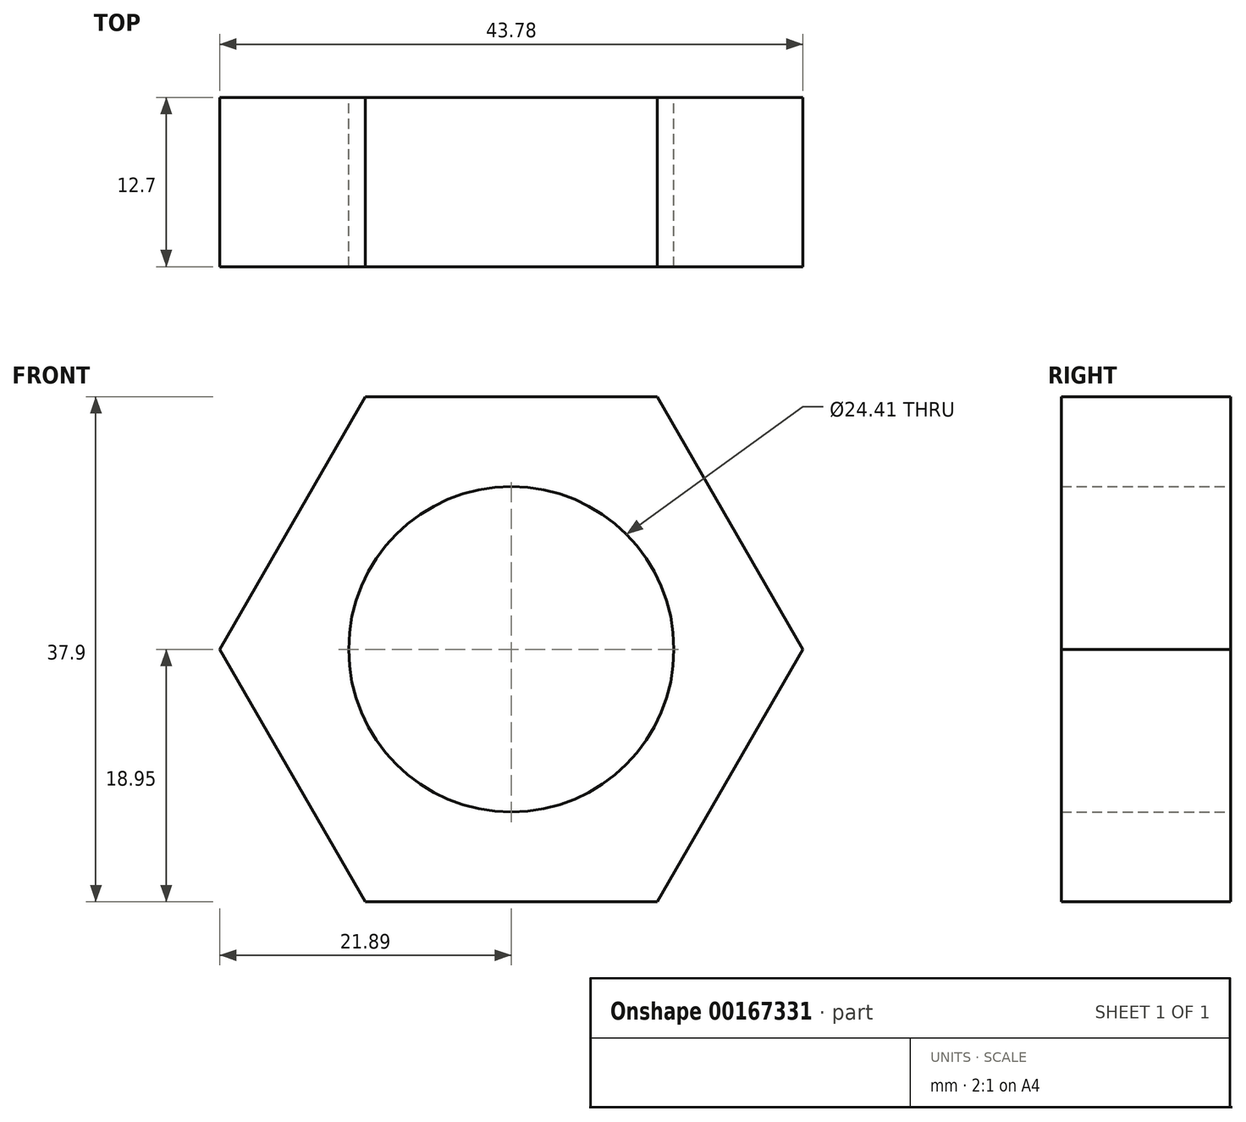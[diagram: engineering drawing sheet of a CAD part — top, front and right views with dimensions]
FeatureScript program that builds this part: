
annotation { "Feature Type Name" : "Feature", "Feature Type Description" : "" }
export const myFeature = defineFeature(function(context is Context, id is Id, definition is map)
    precondition{}
    {
        {
            var Q0;
            Q0=qCreatedBy(makeId("Front.planeOp"),FACE);
            var sketch = newSketch(context, id + "F0", { "sketchPlane" : qUnion([Q0])});
            skCircle(sketch, "E0.cCircle", {"center": v(0, 0) * mm, "radius": 18.95 * mm, "construction": true});
            skLineSegment(sketch, "E0.0", {"start": v(-10.94, 18.95) * mm, "end": v(10.94, 18.95) * mm});
            skLineSegment(sketch, "E0.1", {"start": v(10.94, 18.95) * mm, "end": v(21.89, 0) * mm});
            skLineSegment(sketch, "E0.2", {"start": v(21.89, 0) * mm, "end": v(10.94, -18.95) * mm});
            skLineSegment(sketch, "E0.3", {"start": v(10.94, -18.95) * mm, "end": v(-10.94, -18.95) * mm});
            skLineSegment(sketch, "E0.4", {"start": v(-10.94, -18.95) * mm, "end": v(-21.89, 0) * mm});
            skLineSegment(sketch, "E0.5", {"start": v(-21.89, 0) * mm, "end": v(-10.94, 18.95) * mm});
            skPoint(sketch, "E0.0.midPoint", {"position": v(0, 18.95) * mm});
            skCircle(sketch, "E1", {"center": v(0, 0) * mm, "radius": 12.2 * mm});
            skSolve(sketch);
        }
        {
            var Q0;
            Q0 = qSketchRegion(id + "F0", true);
            extrude(context, id + "F1", {"entities" : qUnion([Q0]), "depth" : 12.7 * mm});
        }
    });
